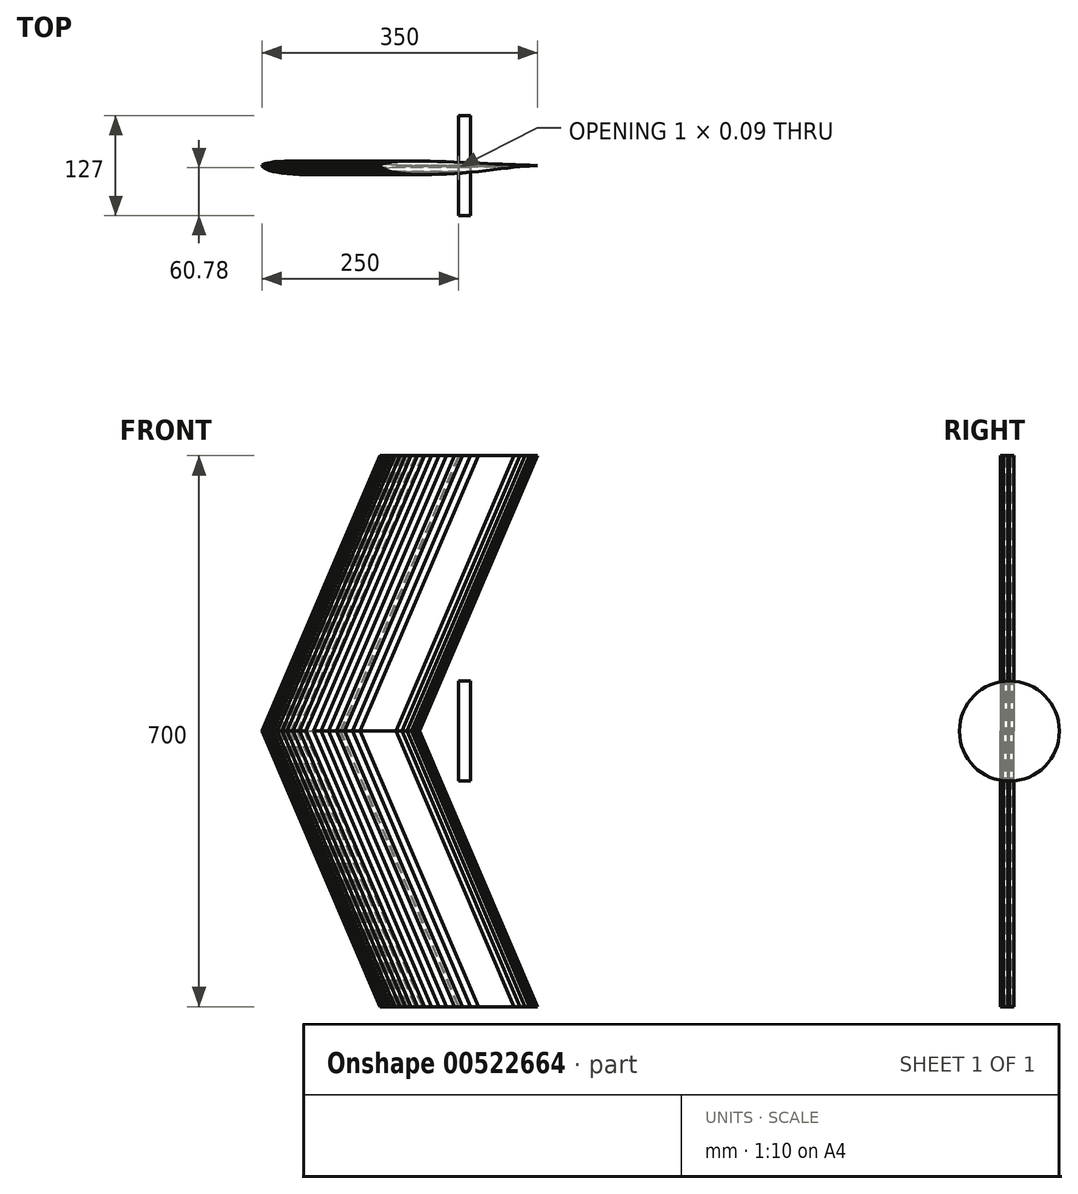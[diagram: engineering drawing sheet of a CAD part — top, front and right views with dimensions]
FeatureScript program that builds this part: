
annotation { "Feature Type Name" : "Feature", "Feature Type Description" : "" }
export const myFeature = defineFeature(function(context is Context, id is Id, definition is map)
    precondition{}
    {
        {
            var Q0;
            Q0=qCreatedBy(makeId("Top.planeOp"),FACE);
            var sketch = newSketch(context, id + "F0", { "sketchPlane" : qUnion([Q0])});
            skLineSegment(sketch, "E0", {"start": v(0.5, 0.01) * mm, "end": v(0.5, 0.01) * mm});
            skLineSegment(sketch, "E1", {"start": v(0.5, 0.01) * mm, "end": v(0.49, 0.01) * mm});
            skLineSegment(sketch, "E2", {"start": v(0.49, 0.01) * mm, "end": v(0.47, 0.01) * mm});
            skLineSegment(sketch, "E3", {"start": v(0.47, 0.01) * mm, "end": v(0.45, 0.01) * mm});
            skLineSegment(sketch, "E4", {"start": v(0.45, 0.01) * mm, "end": v(0.42, 0) * mm});
            skLineSegment(sketch, "E5", {"start": v(0.42, 0) * mm, "end": v(0.39, 0) * mm});
            skLineSegment(sketch, "E6", {"start": v(0.39, 0) * mm, "end": v(0.35, 0) * mm});
            skLineSegment(sketch, "E7", {"start": v(0.35, 0) * mm, "end": v(0.31, 0) * mm});
            skLineSegment(sketch, "E8", {"start": v(0.31, 0) * mm, "end": v(0.27, 0) * mm});
            skLineSegment(sketch, "E9", {"start": v(0.27, 0) * mm, "end": v(0.22, -0.01) * mm});
            skLineSegment(sketch, "E10", {"start": v(0.22, -0.01) * mm, "end": v(0.17, -0.02) * mm});
            skLineSegment(sketch, "E11", {"start": v(0.17, -0.02) * mm, "end": v(0.12, -0.02) * mm});
            skLineSegment(sketch, "E12", {"start": v(0.12, -0.02) * mm, "end": v(0.07, -0.03) * mm});
            skLineSegment(sketch, "E13", {"start": v(0.07, -0.03) * mm, "end": v(0.02, -0.03) * mm});
            skLineSegment(sketch, "E14", {"start": v(0.02, -0.03) * mm, "end": v(-0.03, -0.04) * mm});
            skLineSegment(sketch, "E15", {"start": v(-0.03, -0.04) * mm, "end": v(-0.08, -0.04) * mm});
            skLineSegment(sketch, "E16", {"start": v(-0.08, -0.04) * mm, "end": v(-0.13, -0.04) * mm});
            skLineSegment(sketch, "E17", {"start": v(-0.13, -0.04) * mm, "end": v(-0.17, -0.04) * mm});
            skLineSegment(sketch, "E18", {"start": v(-0.17, -0.04) * mm, "end": v(-0.22, -0.04) * mm});
            skLineSegment(sketch, "E19", {"start": v(-0.22, -0.04) * mm, "end": v(-0.26, -0.04) * mm});
            skLineSegment(sketch, "E20", {"start": v(-0.26, -0.04) * mm, "end": v(-0.3, -0.04) * mm});
            skLineSegment(sketch, "E21", {"start": v(-0.3, -0.04) * mm, "end": v(-0.34, -0.04) * mm});
            skLineSegment(sketch, "E22", {"start": v(-0.34, -0.04) * mm, "end": v(-0.37, -0.03) * mm});
            skLineSegment(sketch, "E23", {"start": v(-0.37, -0.03) * mm, "end": v(-0.4, -0.03) * mm});
            skLineSegment(sketch, "E24", {"start": v(-0.4, -0.03) * mm, "end": v(-0.43, -0.02) * mm});
            skLineSegment(sketch, "E25", {"start": v(-0.43, -0.02) * mm, "end": v(-0.45, -0.02) * mm});
            skLineSegment(sketch, "E26", {"start": v(-0.45, -0.02) * mm, "end": v(-0.47, -0.01) * mm});
            skLineSegment(sketch, "E27", {"start": v(-0.47, -0.01) * mm, "end": v(-0.48, 0) * mm});
            skLineSegment(sketch, "E28", {"start": v(-0.48, 0) * mm, "end": v(-0.5, 0) * mm});
            skLineSegment(sketch, "E29", {"start": v(-0.5, 0) * mm, "end": v(-0.5, 0.01) * mm});
            skLineSegment(sketch, "E30", {"start": v(-0.5, 0.01) * mm, "end": v(-0.5, 0.01) * mm});
            skLineSegment(sketch, "E31", {"start": v(-0.5, 0.01) * mm, "end": v(-0.5, 0.02) * mm});
            skLineSegment(sketch, "E32", {"start": v(-0.5, 0.02) * mm, "end": v(-0.5, 0.02) * mm});
            skLineSegment(sketch, "E33", {"start": v(-0.5, 0.02) * mm, "end": v(-0.48, 0.03) * mm});
            skLineSegment(sketch, "E34", {"start": v(-0.48, 0.03) * mm, "end": v(-0.47, 0.03) * mm});
            skLineSegment(sketch, "E35", {"start": v(-0.47, 0.03) * mm, "end": v(-0.44, 0.03) * mm});
            skLineSegment(sketch, "E36", {"start": v(-0.44, 0.03) * mm, "end": v(-0.42, 0.04) * mm});
            skLineSegment(sketch, "E37", {"start": v(-0.42, 0.04) * mm, "end": v(-0.39, 0.04) * mm});
            skLineSegment(sketch, "E38", {"start": v(-0.39, 0.04) * mm, "end": v(-0.35, 0.04) * mm});
            skLineSegment(sketch, "E39", {"start": v(-0.35, 0.04) * mm, "end": v(-0.32, 0.04) * mm});
            skLineSegment(sketch, "E40", {"start": v(-0.32, 0.04) * mm, "end": v(-0.28, 0.04) * mm});
            skLineSegment(sketch, "E41", {"start": v(-0.28, 0.04) * mm, "end": v(-0.23, 0.04) * mm});
            skLineSegment(sketch, "E42", {"start": v(-0.23, 0.04) * mm, "end": v(-0.18, 0.04) * mm});
            skLineSegment(sketch, "E43", {"start": v(-0.18, 0.04) * mm, "end": v(-0.13, 0.04) * mm});
            skLineSegment(sketch, "E44", {"start": v(-0.13, 0.04) * mm, "end": v(-0.08, 0.04) * mm});
            skLineSegment(sketch, "E45", {"start": v(-0.08, 0.04) * mm, "end": v(-0.03, 0.04) * mm});
            skLineSegment(sketch, "E46", {"start": v(-0.03, 0.04) * mm, "end": v(0.02, 0.03) * mm});
            skLineSegment(sketch, "E47", {"start": v(0.02, 0.03) * mm, "end": v(0.08, 0.03) * mm});
            skLineSegment(sketch, "E48", {"start": v(0.08, 0.03) * mm, "end": v(0.13, 0.03) * mm});
            skLineSegment(sketch, "E49", {"start": v(0.13, 0.03) * mm, "end": v(0.18, 0.03) * mm});
            skLineSegment(sketch, "E50", {"start": v(0.18, 0.03) * mm, "end": v(0.23, 0.02) * mm});
            skLineSegment(sketch, "E51", {"start": v(0.23, 0.02) * mm, "end": v(0.28, 0.02) * mm});
            skLineSegment(sketch, "E52", {"start": v(0.28, 0.02) * mm, "end": v(0.32, 0.02) * mm});
            skLineSegment(sketch, "E53", {"start": v(0.32, 0.02) * mm, "end": v(0.36, 0.02) * mm});
            skLineSegment(sketch, "E54", {"start": v(0.36, 0.02) * mm, "end": v(0.4, 0.02) * mm});
            skLineSegment(sketch, "E55", {"start": v(0.4, 0.02) * mm, "end": v(0.43, 0.02) * mm});
            skLineSegment(sketch, "E56", {"start": v(0.43, 0.02) * mm, "end": v(0.45, 0.02) * mm});
            skLineSegment(sketch, "E57", {"start": v(0.45, 0.02) * mm, "end": v(0.47, 0.01) * mm});
            skLineSegment(sketch, "E58", {"start": v(0.47, 0.01) * mm, "end": v(0.49, 0.01) * mm});
            skLineSegment(sketch, "E59", {"start": v(0.49, 0.01) * mm, "end": v(0.5, 0.01) * mm});
            skLineSegment(sketch, "E60", {"start": v(0.5, 0.01) * mm, "end": v(-0.5, 0.01) * mm});
            skLineSegment(sketch, "E61", {"start": v(100, 2.68) * mm, "end": v(99.36, 2.68) * mm});
            skLineSegment(sketch, "E62", {"start": v(99.36, 2.68) * mm, "end": v(97.42, 2.67) * mm});
            skLineSegment(sketch, "E63", {"start": v(97.42, 2.67) * mm, "end": v(94.22, 2.56) * mm});
            skLineSegment(sketch, "E64", {"start": v(94.22, 2.56) * mm, "end": v(89.83, 2.32) * mm});
            skLineSegment(sketch, "E65", {"start": v(89.83, 2.32) * mm, "end": v(84.34, 1.93) * mm});
            skLineSegment(sketch, "E66", {"start": v(84.34, 1.93) * mm, "end": v(77.83, 1.36) * mm});
            skLineSegment(sketch, "E67", {"start": v(77.83, 1.36) * mm, "end": v(70.45, 0.6) * mm});
            skLineSegment(sketch, "E68", {"start": v(70.45, 0.6) * mm, "end": v(62.32, -0.32) * mm});
            skLineSegment(sketch, "E69", {"start": v(62.32, -0.32) * mm, "end": v(53.57, -1.36) * mm});
            skLineSegment(sketch, "E70", {"start": v(53.57, -1.36) * mm, "end": v(44.33, -2.48) * mm});
            skLineSegment(sketch, "E71", {"start": v(44.33, -2.48) * mm, "end": v(34.73, -3.63) * mm});
            skLineSegment(sketch, "E72", {"start": v(34.73, -3.63) * mm, "end": v(24.87, -4.75) * mm});
            skLineSegment(sketch, "E73", {"start": v(24.87, -4.75) * mm, "end": v(14.85, -5.77) * mm});
            skLineSegment(sketch, "E74", {"start": v(14.85, -5.77) * mm, "end": v(4.75, -6.66) * mm});
            skLineSegment(sketch, "E75", {"start": v(4.75, -6.66) * mm, "end": v(-5.34, -7.4) * mm});
            skLineSegment(sketch, "E76", {"start": v(-5.34, -7.4) * mm, "end": v(-15.33, -8) * mm});
            skLineSegment(sketch, "E77", {"start": v(-15.33, -8) * mm, "end": v(-25.13, -8.4) * mm});
            skLineSegment(sketch, "E78", {"start": v(-25.13, -8.4) * mm, "end": v(-34.63, -8.63) * mm});
            skLineSegment(sketch, "E79", {"start": v(-34.63, -8.63) * mm, "end": v(-43.74, -8.67) * mm});
            skLineSegment(sketch, "E80", {"start": v(-43.74, -8.67) * mm, "end": v(-52.37, -8.5) * mm});
            skLineSegment(sketch, "E81", {"start": v(-52.37, -8.5) * mm, "end": v(-60.45, -8.12) * mm});
            skLineSegment(sketch, "E82", {"start": v(-60.45, -8.12) * mm, "end": v(-67.91, -7.54) * mm});
            skLineSegment(sketch, "E83", {"start": v(-67.91, -7.54) * mm, "end": v(-74.7, -6.75) * mm});
            skLineSegment(sketch, "E84", {"start": v(-74.7, -6.75) * mm, "end": v(-80.75, -5.79) * mm});
            skLineSegment(sketch, "E85", {"start": v(-80.75, -5.79) * mm, "end": v(-86.02, -4.65) * mm});
            skLineSegment(sketch, "E86", {"start": v(-86.02, -4.65) * mm, "end": v(-90.48, -3.38) * mm});
            skLineSegment(sketch, "E87", {"start": v(-90.48, -3.38) * mm, "end": v(-94.1, -2) * mm});
            skLineSegment(sketch, "E88", {"start": v(-94.1, -2) * mm, "end": v(-96.89, -0.55) * mm});
            skLineSegment(sketch, "E89", {"start": v(-96.89, -0.55) * mm, "end": v(-98.82, 0.87) * mm});
            skLineSegment(sketch, "E90", {"start": v(-98.82, 0.87) * mm, "end": v(-99.88, 2.17) * mm});
            skLineSegment(sketch, "E91", {"start": v(-99.88, 2.17) * mm, "end": v(-100, 2.68) * mm});
            skLineSegment(sketch, "E92", {"start": v(-100, 2.68) * mm, "end": v(-99.84, 3.2) * mm});
            skLineSegment(sketch, "E93", {"start": v(-99.84, 3.2) * mm, "end": v(-98.62, 4.13) * mm});
            skLineSegment(sketch, "E94", {"start": v(-98.62, 4.13) * mm, "end": v(-96.34, 5.08) * mm});
            skLineSegment(sketch, "E95", {"start": v(-96.34, 5.08) * mm, "end": v(-93.07, 5.98) * mm});
            skLineSegment(sketch, "E96", {"start": v(-93.07, 5.98) * mm, "end": v(-88.87, 6.8) * mm});
            skLineSegment(sketch, "E97", {"start": v(-88.87, 6.8) * mm, "end": v(-83.76, 7.5) * mm});
            skLineSegment(sketch, "E98", {"start": v(-83.76, 7.5) * mm, "end": v(-77.79, 8.05) * mm});
            skLineSegment(sketch, "E99", {"start": v(-77.79, 8.05) * mm, "end": v(-71, 8.43) * mm});
            skLineSegment(sketch, "E100", {"start": v(-71, 8.43) * mm, "end": v(-63.41, 8.63) * mm});
            skLineSegment(sketch, "E101", {"start": v(-63.41, 8.63) * mm, "end": v(-55.1, 8.67) * mm});
            skLineSegment(sketch, "E102", {"start": v(-55.1, 8.67) * mm, "end": v(-46.16, 8.57) * mm});
            skLineSegment(sketch, "E103", {"start": v(-46.16, 8.57) * mm, "end": v(-36.64, 8.35) * mm});
            skLineSegment(sketch, "E104", {"start": v(-36.64, 8.35) * mm, "end": v(-26.67, 8.03) * mm});
            skLineSegment(sketch, "E105", {"start": v(-26.67, 8.03) * mm, "end": v(-16.34, 7.64) * mm});
            skLineSegment(sketch, "E106", {"start": v(-16.34, 7.64) * mm, "end": v(-5.78, 7.19) * mm});
            skLineSegment(sketch, "E107", {"start": v(-5.78, 7.19) * mm, "end": v(4.9, 6.71) * mm});
            skLineSegment(sketch, "E108", {"start": v(4.9, 6.71) * mm, "end": v(15.57, 6.23) * mm});
            skLineSegment(sketch, "E109", {"start": v(15.57, 6.23) * mm, "end": v(26.09, 5.76) * mm});
            skLineSegment(sketch, "E110", {"start": v(26.09, 5.76) * mm, "end": v(36.33, 5.3) * mm});
            skLineSegment(sketch, "E111", {"start": v(36.33, 5.3) * mm, "end": v(46.17, 4.88) * mm});
            skLineSegment(sketch, "E112", {"start": v(46.17, 4.88) * mm, "end": v(55.5, 4.48) * mm});
            skLineSegment(sketch, "E113", {"start": v(55.5, 4.48) * mm, "end": v(64.18, 4.13) * mm});
            skLineSegment(sketch, "E114", {"start": v(64.18, 4.13) * mm, "end": v(72.12, 3.82) * mm});
            skLineSegment(sketch, "E115", {"start": v(72.12, 3.82) * mm, "end": v(79.21, 3.55) * mm});
            skLineSegment(sketch, "E116", {"start": v(79.21, 3.55) * mm, "end": v(85.38, 3.33) * mm});
            skLineSegment(sketch, "E117", {"start": v(85.38, 3.33) * mm, "end": v(90.53, 3.14) * mm});
            skLineSegment(sketch, "E118", {"start": v(90.53, 3.14) * mm, "end": v(94.6, 2.98) * mm});
            skLineSegment(sketch, "E119", {"start": v(94.6, 2.98) * mm, "end": v(97.55, 2.83) * mm});
            skLineSegment(sketch, "E120", {"start": v(97.55, 2.83) * mm, "end": v(99.37, 2.72) * mm});
            skLineSegment(sketch, "E121", {"start": v(99.37, 2.72) * mm, "end": v(100, 2.68) * mm});
            skSolve(sketch);
        }
        {
            var Q0;
            Q0=qCreatedBy(makeId("Front.planeOp"),FACE);
            var sketch = newSketch(context, id + "F1", { "sketchPlane" : qUnion([Q0])});
            skLineSegment(sketch, "E122", {"start": v(0, 0) * mm, "end": v(0, 350) * mm});
            skLineSegment(sketch, "E123", {"start": v(0, 0) * mm, "end": v(0, 350) * mm, "construction": true});
            skLineSegment(sketch, "E124", {"start": v(0, 0) * mm, "end": v(-150, 350) * mm});
            skSolve(sketch);
        }
        {
            var Q0;
            Q0 = qSketchRegion(id + "F0", true);
            var Q1;
            Q1=sQuery(id+"F1.wireOp",EDGE,"E124");
            sweep(context, id + "F2", {"profiles" : qUnion([Q0]), "path" : qUnion([Q1])});
        }
        {
            var Q0;
            Q0=makeQuery(id+"F2.opSweep","SWEPT_BODY",BODY,{"disambiguationData":[OSD([sQuery(id+"F0.wireOp",EDGE,"E2"),sQuery(id+"F0.wireOp",EDGE,"E3"),sQuery(id+"F0.wireOp",EDGE,"E4"),sQuery(id+"F0.wireOp",EDGE,"E5"),sQuery(id+"F0.wireOp",EDGE,"E6"),sQuery(id+"F0.wireOp",EDGE,"E7"),sQuery(id+"F0.wireOp",EDGE,"E8"),sQuery(id+"F0.wireOp",EDGE,"E9"),sQuery(id+"F0.wireOp",EDGE,"E10"),sQuery(id+"F0.wireOp",EDGE,"E11"),sQuery(id+"F0.wireOp",EDGE,"E12"),sQuery(id+"F0.wireOp",EDGE,"E13"),sQuery(id+"F0.wireOp",EDGE,"E14"),sQuery(id+"F0.wireOp",EDGE,"E15"),sQuery(id+"F0.wireOp",EDGE,"E16"),sQuery(id+"F0.wireOp",EDGE,"E17"),sQuery(id+"F0.wireOp",EDGE,"E18"),sQuery(id+"F0.wireOp",EDGE,"E19"),sQuery(id+"F0.wireOp",EDGE,"E20"),sQuery(id+"F0.wireOp",EDGE,"E21"),sQuery(id+"F0.wireOp",EDGE,"E22"),sQuery(id+"F0.wireOp",EDGE,"E23"),sQuery(id+"F0.wireOp",EDGE,"E24"),sQuery(id+"F0.wireOp",EDGE,"E25"),sQuery(id+"F0.wireOp",EDGE,"E26"),sQuery(id+"F0.wireOp",EDGE,"E27"),sQuery(id+"F0.wireOp",EDGE,"E28"),sQuery(id+"F0.wireOp",EDGE,"E29"),sQuery(id+"F0.wireOp",EDGE,"E30"),sQuery(id+"F0.wireOp",EDGE,"E31"),sQuery(id+"F0.wireOp",EDGE,"E32"),sQuery(id+"F0.wireOp",EDGE,"E33"),sQuery(id+"F0.wireOp",EDGE,"E34"),sQuery(id+"F0.wireOp",EDGE,"E35"),sQuery(id+"F0.wireOp",EDGE,"E36"),sQuery(id+"F0.wireOp",EDGE,"E37"),sQuery(id+"F0.wireOp",EDGE,"E38"),sQuery(id+"F0.wireOp",EDGE,"E39"),sQuery(id+"F0.wireOp",EDGE,"E40"),sQuery(id+"F0.wireOp",EDGE,"E41"),sQuery(id+"F0.wireOp",EDGE,"E42"),sQuery(id+"F0.wireOp",EDGE,"E43"),sQuery(id+"F0.wireOp",EDGE,"E44"),sQuery(id+"F0.wireOp",EDGE,"E45"),sQuery(id+"F0.wireOp",EDGE,"E46"),sQuery(id+"F0.wireOp",EDGE,"E47"),sQuery(id+"F0.wireOp",EDGE,"E48"),sQuery(id+"F0.wireOp",EDGE,"E49"),sQuery(id+"F0.wireOp",EDGE,"E50"),sQuery(id+"F0.wireOp",EDGE,"E51"),sQuery(id+"F0.wireOp",EDGE,"E52"),sQuery(id+"F0.wireOp",EDGE,"E53"),sQuery(id+"F0.wireOp",EDGE,"E54"),sQuery(id+"F0.wireOp",EDGE,"E55"),sQuery(id+"F0.wireOp",EDGE,"E56"),sQuery(id+"F0.wireOp",EDGE,"E57"),sQuery(id+"F0.wireOp",EDGE,"E58"),sQuery(id+"F0.wireOp",EDGE,"E59"),sQuery(id+"F0.wireOp",EDGE,"E0"),sQuery(id+"F0.wireOp",EDGE,"E60"),sQuery(id+"F0.wireOp",EDGE,"E61"),sQuery(id+"F0.wireOp",EDGE,"E62"),sQuery(id+"F0.wireOp",EDGE,"E63"),sQuery(id+"F0.wireOp",EDGE,"E64"),sQuery(id+"F0.wireOp",EDGE,"E65"),sQuery(id+"F0.wireOp",EDGE,"E66"),sQuery(id+"F0.wireOp",EDGE,"E67"),sQuery(id+"F0.wireOp",EDGE,"E68"),sQuery(id+"F0.wireOp",EDGE,"E69"),sQuery(id+"F0.wireOp",EDGE,"E70"),sQuery(id+"F0.wireOp",EDGE,"E71"),sQuery(id+"F0.wireOp",EDGE,"E72"),sQuery(id+"F0.wireOp",EDGE,"E73"),sQuery(id+"F0.wireOp",EDGE,"E74"),sQuery(id+"F0.wireOp",EDGE,"E75"),sQuery(id+"F0.wireOp",EDGE,"E76"),sQuery(id+"F0.wireOp",EDGE,"E77"),sQuery(id+"F0.wireOp",EDGE,"E78"),sQuery(id+"F0.wireOp",EDGE,"E79"),sQuery(id+"F0.wireOp",EDGE,"E80"),sQuery(id+"F0.wireOp",EDGE,"E81"),sQuery(id+"F0.wireOp",EDGE,"E82"),sQuery(id+"F0.wireOp",EDGE,"E83"),sQuery(id+"F0.wireOp",EDGE,"E84"),sQuery(id+"F0.wireOp",EDGE,"E85"),sQuery(id+"F0.wireOp",EDGE,"E86"),sQuery(id+"F0.wireOp",EDGE,"E87"),sQuery(id+"F0.wireOp",EDGE,"E88"),sQuery(id+"F0.wireOp",EDGE,"E89"),sQuery(id+"F0.wireOp",EDGE,"E90"),sQuery(id+"F0.wireOp",EDGE,"E91"),sQuery(id+"F0.wireOp",EDGE,"E92"),sQuery(id+"F0.wireOp",EDGE,"E93"),sQuery(id+"F0.wireOp",EDGE,"E94"),sQuery(id+"F0.wireOp",EDGE,"E95"),sQuery(id+"F0.wireOp",EDGE,"E96"),sQuery(id+"F0.wireOp",EDGE,"E97"),sQuery(id+"F0.wireOp",EDGE,"E98"),sQuery(id+"F0.wireOp",EDGE,"E99"),sQuery(id+"F0.wireOp",EDGE,"E100"),sQuery(id+"F0.wireOp",EDGE,"E101"),sQuery(id+"F0.wireOp",EDGE,"E102"),sQuery(id+"F0.wireOp",EDGE,"E103"),sQuery(id+"F0.wireOp",EDGE,"E104"),sQuery(id+"F0.wireOp",EDGE,"E105"),sQuery(id+"F0.wireOp",EDGE,"E106"),sQuery(id+"F0.wireOp",EDGE,"E107"),sQuery(id+"F0.wireOp",EDGE,"E108"),sQuery(id+"F0.wireOp",EDGE,"E109"),sQuery(id+"F0.wireOp",EDGE,"E110"),sQuery(id+"F0.wireOp",EDGE,"E111"),sQuery(id+"F0.wireOp",EDGE,"E112"),sQuery(id+"F0.wireOp",EDGE,"E113"),sQuery(id+"F0.wireOp",EDGE,"E114"),sQuery(id+"F0.wireOp",EDGE,"E115"),sQuery(id+"F0.wireOp",EDGE,"E116"),sQuery(id+"F0.wireOp",EDGE,"E117"),sQuery(id+"F0.wireOp",EDGE,"E118"),sQuery(id+"F0.wireOp",EDGE,"E119"),sQuery(id+"F0.wireOp",EDGE,"E120"),sQuery(id+"F0.wireOp",EDGE,"E121"),sQuery(id+"F1.wireOp",EDGE,"E124")])]});
            var Q1;
            Q1=makeQuery(id+"F2.opSweep","CAP_FACE",FACE,{"disambiguationData":[OSD([sQuery(id+"F0.wireOp",EDGE,"E2"),sQuery(id+"F0.wireOp",EDGE,"E3"),sQuery(id+"F0.wireOp",EDGE,"E4"),sQuery(id+"F0.wireOp",EDGE,"E5"),sQuery(id+"F0.wireOp",EDGE,"E6"),sQuery(id+"F0.wireOp",EDGE,"E7"),sQuery(id+"F0.wireOp",EDGE,"E8"),sQuery(id+"F0.wireOp",EDGE,"E9"),sQuery(id+"F0.wireOp",EDGE,"E10"),sQuery(id+"F0.wireOp",EDGE,"E11"),sQuery(id+"F0.wireOp",EDGE,"E12"),sQuery(id+"F0.wireOp",EDGE,"E13"),sQuery(id+"F0.wireOp",EDGE,"E14"),sQuery(id+"F0.wireOp",EDGE,"E15"),sQuery(id+"F0.wireOp",EDGE,"E16"),sQuery(id+"F0.wireOp",EDGE,"E17"),sQuery(id+"F0.wireOp",EDGE,"E18"),sQuery(id+"F0.wireOp",EDGE,"E19"),sQuery(id+"F0.wireOp",EDGE,"E20"),sQuery(id+"F0.wireOp",EDGE,"E21"),sQuery(id+"F0.wireOp",EDGE,"E22"),sQuery(id+"F0.wireOp",EDGE,"E23"),sQuery(id+"F0.wireOp",EDGE,"E24"),sQuery(id+"F0.wireOp",EDGE,"E25"),sQuery(id+"F0.wireOp",EDGE,"E26"),sQuery(id+"F0.wireOp",EDGE,"E27"),sQuery(id+"F0.wireOp",EDGE,"E28"),sQuery(id+"F0.wireOp",EDGE,"E29"),sQuery(id+"F0.wireOp",EDGE,"E30"),sQuery(id+"F0.wireOp",EDGE,"E31"),sQuery(id+"F0.wireOp",EDGE,"E32"),sQuery(id+"F0.wireOp",EDGE,"E33"),sQuery(id+"F0.wireOp",EDGE,"E34"),sQuery(id+"F0.wireOp",EDGE,"E35"),sQuery(id+"F0.wireOp",EDGE,"E36"),sQuery(id+"F0.wireOp",EDGE,"E37"),sQuery(id+"F0.wireOp",EDGE,"E38"),sQuery(id+"F0.wireOp",EDGE,"E39"),sQuery(id+"F0.wireOp",EDGE,"E40"),sQuery(id+"F0.wireOp",EDGE,"E41"),sQuery(id+"F0.wireOp",EDGE,"E42"),sQuery(id+"F0.wireOp",EDGE,"E43"),sQuery(id+"F0.wireOp",EDGE,"E44"),sQuery(id+"F0.wireOp",EDGE,"E45"),sQuery(id+"F0.wireOp",EDGE,"E46"),sQuery(id+"F0.wireOp",EDGE,"E47"),sQuery(id+"F0.wireOp",EDGE,"E48"),sQuery(id+"F0.wireOp",EDGE,"E49"),sQuery(id+"F0.wireOp",EDGE,"E50"),sQuery(id+"F0.wireOp",EDGE,"E51"),sQuery(id+"F0.wireOp",EDGE,"E52"),sQuery(id+"F0.wireOp",EDGE,"E53"),sQuery(id+"F0.wireOp",EDGE,"E54"),sQuery(id+"F0.wireOp",EDGE,"E55"),sQuery(id+"F0.wireOp",EDGE,"E56"),sQuery(id+"F0.wireOp",EDGE,"E57"),sQuery(id+"F0.wireOp",EDGE,"E58"),sQuery(id+"F0.wireOp",EDGE,"E59"),sQuery(id+"F0.wireOp",EDGE,"E0"),sQuery(id+"F0.wireOp",EDGE,"E60"),sQuery(id+"F0.wireOp",EDGE,"E61"),sQuery(id+"F0.wireOp",EDGE,"E62"),sQuery(id+"F0.wireOp",EDGE,"E63"),sQuery(id+"F0.wireOp",EDGE,"E64"),sQuery(id+"F0.wireOp",EDGE,"E65"),sQuery(id+"F0.wireOp",EDGE,"E66"),sQuery(id+"F0.wireOp",EDGE,"E67"),sQuery(id+"F0.wireOp",EDGE,"E68"),sQuery(id+"F0.wireOp",EDGE,"E69"),sQuery(id+"F0.wireOp",EDGE,"E70"),sQuery(id+"F0.wireOp",EDGE,"E71"),sQuery(id+"F0.wireOp",EDGE,"E72"),sQuery(id+"F0.wireOp",EDGE,"E73"),sQuery(id+"F0.wireOp",EDGE,"E74"),sQuery(id+"F0.wireOp",EDGE,"E75"),sQuery(id+"F0.wireOp",EDGE,"E76"),sQuery(id+"F0.wireOp",EDGE,"E77"),sQuery(id+"F0.wireOp",EDGE,"E78"),sQuery(id+"F0.wireOp",EDGE,"E79"),sQuery(id+"F0.wireOp",EDGE,"E80"),sQuery(id+"F0.wireOp",EDGE,"E81"),sQuery(id+"F0.wireOp",EDGE,"E82"),sQuery(id+"F0.wireOp",EDGE,"E83"),sQuery(id+"F0.wireOp",EDGE,"E84"),sQuery(id+"F0.wireOp",EDGE,"E85"),sQuery(id+"F0.wireOp",EDGE,"E86"),sQuery(id+"F0.wireOp",EDGE,"E87"),sQuery(id+"F0.wireOp",EDGE,"E88"),sQuery(id+"F0.wireOp",EDGE,"E89"),sQuery(id+"F0.wireOp",EDGE,"E90"),sQuery(id+"F0.wireOp",EDGE,"E91"),sQuery(id+"F0.wireOp",EDGE,"E92"),sQuery(id+"F0.wireOp",EDGE,"E93"),sQuery(id+"F0.wireOp",EDGE,"E94"),sQuery(id+"F0.wireOp",EDGE,"E95"),sQuery(id+"F0.wireOp",EDGE,"E96"),sQuery(id+"F0.wireOp",EDGE,"E97"),sQuery(id+"F0.wireOp",EDGE,"E98"),sQuery(id+"F0.wireOp",EDGE,"E99"),sQuery(id+"F0.wireOp",EDGE,"E100"),sQuery(id+"F0.wireOp",EDGE,"E101"),sQuery(id+"F0.wireOp",EDGE,"E102"),sQuery(id+"F0.wireOp",EDGE,"E103"),sQuery(id+"F0.wireOp",EDGE,"E104"),sQuery(id+"F0.wireOp",EDGE,"E105"),sQuery(id+"F0.wireOp",EDGE,"E106"),sQuery(id+"F0.wireOp",EDGE,"E107"),sQuery(id+"F0.wireOp",EDGE,"E108"),sQuery(id+"F0.wireOp",EDGE,"E109"),sQuery(id+"F0.wireOp",EDGE,"E110"),sQuery(id+"F0.wireOp",EDGE,"E111"),sQuery(id+"F0.wireOp",EDGE,"E112"),sQuery(id+"F0.wireOp",EDGE,"E113"),sQuery(id+"F0.wireOp",EDGE,"E114"),sQuery(id+"F0.wireOp",EDGE,"E115"),sQuery(id+"F0.wireOp",EDGE,"E116"),sQuery(id+"F0.wireOp",EDGE,"E117"),sQuery(id+"F0.wireOp",EDGE,"E118"),sQuery(id+"F0.wireOp",EDGE,"E119"),sQuery(id+"F0.wireOp",EDGE,"E120"),sQuery(id+"F0.wireOp",EDGE,"E121"),sQuery(id+"F1.wireOp",VERTEX,"E124.end")])],"isStart":false});
            mirror(context, id + "F3", {"operationType" : NewBodyOperationType.ADD, "entities" : qUnion([Q0]), "mirrorPlane" : qUnion([Q1])});
        }
        {
            var Q0;
            Q0=qCreatedBy(makeId("Right.planeOp"),FACE);
            var sketch = newSketch(context, id + "F4", { "sketchPlane" : qUnion([Q0])});
            skCircle(sketch, "E125", {"center": v(2.72, 350) * mm, "radius": 63.5 * mm});
            skSolve(sketch);
        }
        {
            var Q0;
            Q0=makeQuery(id+"F4.imprint","IMPRINT",FACE,{"disambiguationData":[TD([[makeQuery(id+"F4.imprint","IMPRINT",EDGE,{"derivedFrom":sQuery(id+"F4.wireOp",EDGE,"E125")}),1.0]])]});
            extrude(context, id + "F5", {"entities" : qUnion([Q0]), "depth" : 15 * mm, "offsetDistance" : 25 * mm});
        }
        {
            var Q0;
            Q0=qCreatedBy(makeId("Top.planeOp"),FACE);
            cPlane(context, id + "F6", {"entities" : qUnion([Q0]), "cplaneType" : CPlaneType.OFFSET, "offset" : 350 * mm, "width" : 150 * mm, "height" : 150 * mm});
        }
        {
            var Q0;
            Q0=qCreatedBy(id+"F6.planeOp",FACE);
            cPlane(context, id + "F7", {"entities" : qUnion([Q0]), "cplaneType" : CPlaneType.OFFSET, "offset" : 14.2 * mm, "width" : 150 * mm, "height" : 150 * mm});
        }
        {
            var Q0;
            Q0=qCreatedBy(id+"F7.planeOp",FACE);
            var sketch = newSketch(context, id + "F8", { "sketchPlane" : qUnion([Q0])});
            skLineSegment(sketch, "E126.bottom", {"start": v(-261.78, -24.86) * mm, "end": v(111.46, -24.86) * mm});
            skLineSegment(sketch, "E126.top", {"start": v(-261.78, 30.58) * mm, "end": v(111.46, 30.58) * mm});
            skLineSegment(sketch, "E126.left", {"start": v(-261.78, -24.86) * mm, "end": v(-261.78, 30.58) * mm});
            skLineSegment(sketch, "E126.right", {"start": v(111.46, -24.86) * mm, "end": v(111.46, 30.58) * mm});
            skSolve(sketch);
        }
        {
            var Q0;
            Q0=makeQuery(id+"F8.imprint","IMPRINT",FACE,{"disambiguationData":[TD([[makeQuery(id+"F8.imprint","IMPRINT",EDGE,{"derivedFrom":sQuery(id+"F8.wireOp",EDGE,"E126.bottom")}),1.0]])]});
            extrude(context, id + "F9", {"entities" : qUnion([Q0]), "oppositeDirection" : true, "depth" : 4 * mm, "offsetDistance" : 25 * mm});
        }
        {
            var Q0;
            Q0=makeQuery(id+"F2.opSweep","SWEPT_BODY",BODY,{"disambiguationData":[OSD([sQuery(id+"F0.wireOp",EDGE,"E2"),sQuery(id+"F0.wireOp",EDGE,"E3"),sQuery(id+"F0.wireOp",EDGE,"E4"),sQuery(id+"F0.wireOp",EDGE,"E5"),sQuery(id+"F0.wireOp",EDGE,"E6"),sQuery(id+"F0.wireOp",EDGE,"E7"),sQuery(id+"F0.wireOp",EDGE,"E8"),sQuery(id+"F0.wireOp",EDGE,"E9"),sQuery(id+"F0.wireOp",EDGE,"E10"),sQuery(id+"F0.wireOp",EDGE,"E11"),sQuery(id+"F0.wireOp",EDGE,"E12"),sQuery(id+"F0.wireOp",EDGE,"E13"),sQuery(id+"F0.wireOp",EDGE,"E14"),sQuery(id+"F0.wireOp",EDGE,"E15"),sQuery(id+"F0.wireOp",EDGE,"E16"),sQuery(id+"F0.wireOp",EDGE,"E17"),sQuery(id+"F0.wireOp",EDGE,"E18"),sQuery(id+"F0.wireOp",EDGE,"E19"),sQuery(id+"F0.wireOp",EDGE,"E20"),sQuery(id+"F0.wireOp",EDGE,"E21"),sQuery(id+"F0.wireOp",EDGE,"E22"),sQuery(id+"F0.wireOp",EDGE,"E23"),sQuery(id+"F0.wireOp",EDGE,"E24"),sQuery(id+"F0.wireOp",EDGE,"E25"),sQuery(id+"F0.wireOp",EDGE,"E26"),sQuery(id+"F0.wireOp",EDGE,"E27"),sQuery(id+"F0.wireOp",EDGE,"E28"),sQuery(id+"F0.wireOp",EDGE,"E29"),sQuery(id+"F0.wireOp",EDGE,"E30"),sQuery(id+"F0.wireOp",EDGE,"E31"),sQuery(id+"F0.wireOp",EDGE,"E32"),sQuery(id+"F0.wireOp",EDGE,"E33"),sQuery(id+"F0.wireOp",EDGE,"E34"),sQuery(id+"F0.wireOp",EDGE,"E35"),sQuery(id+"F0.wireOp",EDGE,"E36"),sQuery(id+"F0.wireOp",EDGE,"E37"),sQuery(id+"F0.wireOp",EDGE,"E38"),sQuery(id+"F0.wireOp",EDGE,"E39"),sQuery(id+"F0.wireOp",EDGE,"E40"),sQuery(id+"F0.wireOp",EDGE,"E41"),sQuery(id+"F0.wireOp",EDGE,"E42"),sQuery(id+"F0.wireOp",EDGE,"E43"),sQuery(id+"F0.wireOp",EDGE,"E44"),sQuery(id+"F0.wireOp",EDGE,"E45"),sQuery(id+"F0.wireOp",EDGE,"E46"),sQuery(id+"F0.wireOp",EDGE,"E47"),sQuery(id+"F0.wireOp",EDGE,"E48"),sQuery(id+"F0.wireOp",EDGE,"E49"),sQuery(id+"F0.wireOp",EDGE,"E50"),sQuery(id+"F0.wireOp",EDGE,"E51"),sQuery(id+"F0.wireOp",EDGE,"E52"),sQuery(id+"F0.wireOp",EDGE,"E53"),sQuery(id+"F0.wireOp",EDGE,"E54"),sQuery(id+"F0.wireOp",EDGE,"E55"),sQuery(id+"F0.wireOp",EDGE,"E56"),sQuery(id+"F0.wireOp",EDGE,"E57"),sQuery(id+"F0.wireOp",EDGE,"E58"),sQuery(id+"F0.wireOp",EDGE,"E59"),sQuery(id+"F0.wireOp",EDGE,"E0"),sQuery(id+"F0.wireOp",EDGE,"E60"),sQuery(id+"F0.wireOp",EDGE,"E61"),sQuery(id+"F0.wireOp",EDGE,"E62"),sQuery(id+"F0.wireOp",EDGE,"E63"),sQuery(id+"F0.wireOp",EDGE,"E64"),sQuery(id+"F0.wireOp",EDGE,"E65"),sQuery(id+"F0.wireOp",EDGE,"E66"),sQuery(id+"F0.wireOp",EDGE,"E67"),sQuery(id+"F0.wireOp",EDGE,"E68"),sQuery(id+"F0.wireOp",EDGE,"E69"),sQuery(id+"F0.wireOp",EDGE,"E70"),sQuery(id+"F0.wireOp",EDGE,"E71"),sQuery(id+"F0.wireOp",EDGE,"E72"),sQuery(id+"F0.wireOp",EDGE,"E73"),sQuery(id+"F0.wireOp",EDGE,"E74"),sQuery(id+"F0.wireOp",EDGE,"E75"),sQuery(id+"F0.wireOp",EDGE,"E76"),sQuery(id+"F0.wireOp",EDGE,"E77"),sQuery(id+"F0.wireOp",EDGE,"E78"),sQuery(id+"F0.wireOp",EDGE,"E79"),sQuery(id+"F0.wireOp",EDGE,"E80"),sQuery(id+"F0.wireOp",EDGE,"E81"),sQuery(id+"F0.wireOp",EDGE,"E82"),sQuery(id+"F0.wireOp",EDGE,"E83"),sQuery(id+"F0.wireOp",EDGE,"E84"),sQuery(id+"F0.wireOp",EDGE,"E85"),sQuery(id+"F0.wireOp",EDGE,"E86"),sQuery(id+"F0.wireOp",EDGE,"E87"),sQuery(id+"F0.wireOp",EDGE,"E88"),sQuery(id+"F0.wireOp",EDGE,"E89"),sQuery(id+"F0.wireOp",EDGE,"E90"),sQuery(id+"F0.wireOp",EDGE,"E91"),sQuery(id+"F0.wireOp",EDGE,"E92"),sQuery(id+"F0.wireOp",EDGE,"E93"),sQuery(id+"F0.wireOp",EDGE,"E94"),sQuery(id+"F0.wireOp",EDGE,"E95"),sQuery(id+"F0.wireOp",EDGE,"E96"),sQuery(id+"F0.wireOp",EDGE,"E97"),sQuery(id+"F0.wireOp",EDGE,"E98"),sQuery(id+"F0.wireOp",EDGE,"E99"),sQuery(id+"F0.wireOp",EDGE,"E100"),sQuery(id+"F0.wireOp",EDGE,"E101"),sQuery(id+"F0.wireOp",EDGE,"E102"),sQuery(id+"F0.wireOp",EDGE,"E103"),sQuery(id+"F0.wireOp",EDGE,"E104"),sQuery(id+"F0.wireOp",EDGE,"E105"),sQuery(id+"F0.wireOp",EDGE,"E106"),sQuery(id+"F0.wireOp",EDGE,"E107"),sQuery(id+"F0.wireOp",EDGE,"E108"),sQuery(id+"F0.wireOp",EDGE,"E109"),sQuery(id+"F0.wireOp",EDGE,"E110"),sQuery(id+"F0.wireOp",EDGE,"E111"),sQuery(id+"F0.wireOp",EDGE,"E112"),sQuery(id+"F0.wireOp",EDGE,"E113"),sQuery(id+"F0.wireOp",EDGE,"E114"),sQuery(id+"F0.wireOp",EDGE,"E115"),sQuery(id+"F0.wireOp",EDGE,"E116"),sQuery(id+"F0.wireOp",EDGE,"E117"),sQuery(id+"F0.wireOp",EDGE,"E118"),sQuery(id+"F0.wireOp",EDGE,"E119"),sQuery(id+"F0.wireOp",EDGE,"E120"),sQuery(id+"F0.wireOp",EDGE,"E121"),sQuery(id+"F1.wireOp",EDGE,"E124")])]});
            var Q1;
            Q1=makeQuery(id+"F9.opExtrude","SWEPT_BODY",BODY,{"disambiguationData":[OSD([sQuery(id+"F8.wireOp",EDGE,"E126.bottom"),sQuery(id+"F8.wireOp",EDGE,"E126.top"),sQuery(id+"F8.wireOp",EDGE,"E126.left"),sQuery(id+"F8.wireOp",EDGE,"E126.right")])]});
            booleanBodies(context, id + "F10", {"operationType" : BooleanOperationType.SUBTRACTION, "tools" : qUnion([Q0]), "targets" : qUnion([Q1]), "keepTools" : true});
        }
        {
            var Q0;
            Q0=makeQuery(id+"F10.opBoolean","SPLIT",BODY,{"disambiguationData":[OD(0.0)],"derivedFrom":makeQuery(id+"F9.opExtrude","SWEPT_BODY",BODY,{"disambiguationData":[OSD([sQuery(id+"F8.wireOp",EDGE,"E126.bottom"),sQuery(id+"F8.wireOp",EDGE,"E126.top"),sQuery(id+"F8.wireOp",EDGE,"E126.left"),sQuery(id+"F8.wireOp",EDGE,"E126.right")])]})});
            deleteBodies(context, id + "F11", {"entities" : qUnion([Q0])});
        }
    });
